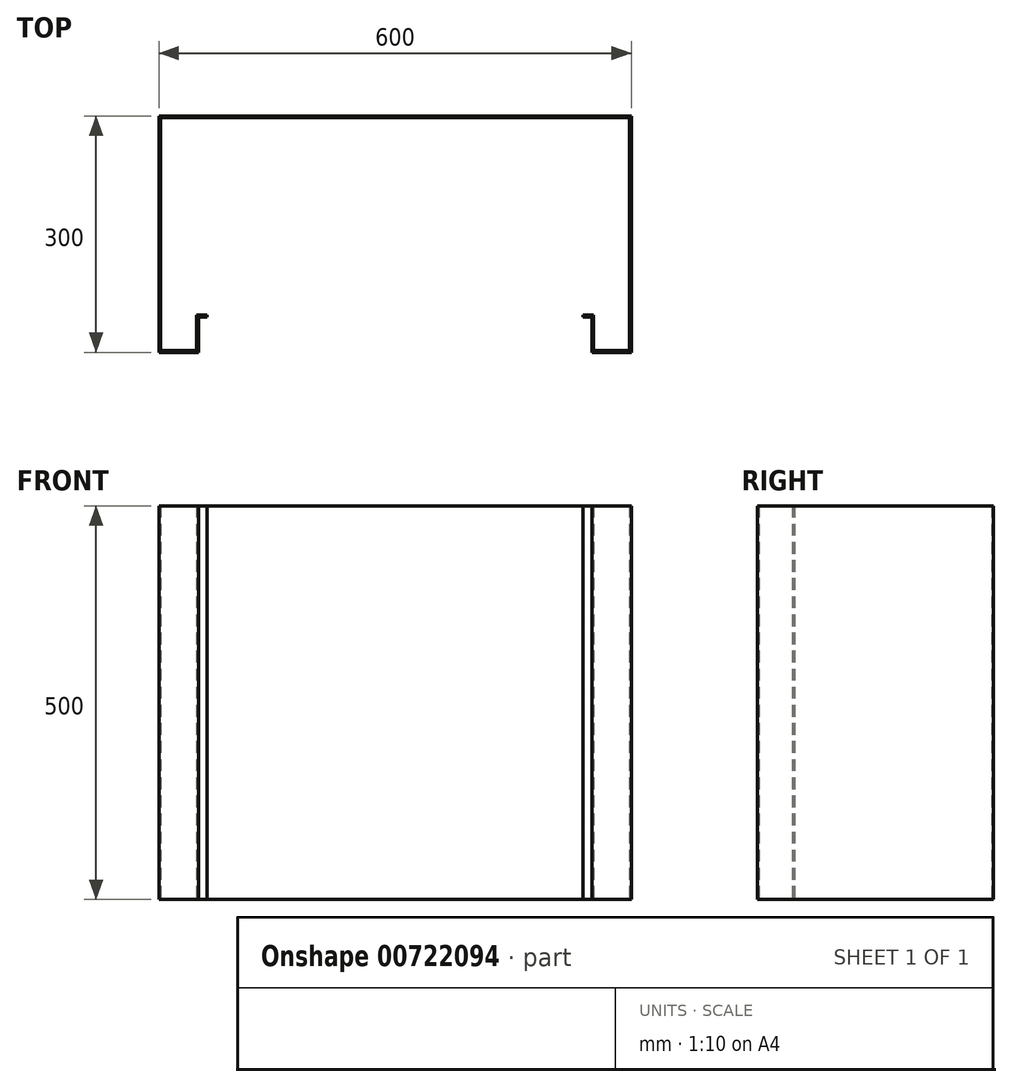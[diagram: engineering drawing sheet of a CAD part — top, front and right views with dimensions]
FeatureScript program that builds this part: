
annotation { "Feature Type Name" : "Feature", "Feature Type Description" : "" }
export const myFeature = defineFeature(function(context is Context, id is Id, definition is map)
    precondition{}
    {
        {
            var Q0;
            Q0=qCreatedBy(makeId("Top.planeOp"),FACE);
            var sketch = newSketch(context, id + "F0", { "sketchPlane" : qUnion([Q0])});
            skLineSegment(sketch, "E0", {"start": v(0, 102.13) * mm, "end": v(-300, 102.13) * mm});
            skLineSegment(sketch, "E1", {"start": v(-300, 102.13) * mm, "end": v(-300, -197.87) * mm});
            skLineSegment(sketch, "E2", {"start": v(-300, -197.87) * mm, "end": v(-250, -197.87) * mm});
            skLineSegment(sketch, "E3", {"start": v(-250, -197.87) * mm, "end": v(-250, -152.87) * mm});
            skLineSegment(sketch, "E4", {"start": v(-250, -152.87) * mm, "end": v(-238.8, -152.87) * mm});
            skLineSegment(sketch, "E5.0", {"start": v(-252, -150.87) * mm, "end": v(-238.8, -150.87) * mm});
            skLineSegment(sketch, "E5.1", {"start": v(-252, -195.87) * mm, "end": v(-252, -150.87) * mm});
            skLineSegment(sketch, "E5.2", {"start": v(-298, -195.87) * mm, "end": v(-252, -195.87) * mm});
            skLineSegment(sketch, "E5.3", {"start": v(-298, 100.13) * mm, "end": v(-298, -195.87) * mm});
            skLineSegment(sketch, "E5.4", {"start": v(0, 100.13) * mm, "end": v(-298, 100.13) * mm});
            skLineSegment(sketch, "E6", {"start": v(-238.8, -152.87) * mm, "end": v(-238.8, -150.87) * mm});
            skLineSegment(sketch, "E7.MirrorCS", {"start": v(252, -150.87) * mm, "end": v(238.8, -150.87) * mm});
            skLineSegment(sketch, "E8.MirrorCS", {"start": v(250, -152.87) * mm, "end": v(238.8, -152.87) * mm});
            skLineSegment(sketch, "E9.MirrorCS", {"start": v(238.8, -152.87) * mm, "end": v(238.8, -150.87) * mm});
            skLineSegment(sketch, "E10.MirrorCS", {"start": v(250, -197.87) * mm, "end": v(250, -152.87) * mm});
            skLineSegment(sketch, "E11.MirrorCS", {"start": v(0, 102.13) * mm, "end": v(300, 102.13) * mm});
            skLineSegment(sketch, "E12.MirrorCS", {"start": v(0, 100.13) * mm, "end": v(298, 100.13) * mm});
            skLineSegment(sketch, "E13.MirrorCS", {"start": v(300, -197.87) * mm, "end": v(250, -197.87) * mm});
            skLineSegment(sketch, "E14.MirrorCS", {"start": v(300, 102.13) * mm, "end": v(300, -197.87) * mm});
            skLineSegment(sketch, "E15.MirrorCS", {"start": v(298, -195.87) * mm, "end": v(252, -195.87) * mm});
            skLineSegment(sketch, "E16.MirrorCS", {"start": v(298, 100.13) * mm, "end": v(298, -195.87) * mm});
            skLineSegment(sketch, "E17.MirrorCS", {"start": v(252, -195.87) * mm, "end": v(252, -150.87) * mm});
            skSolve(sketch);
        }
        {
            var Q0;
            Q0 = qSketchRegion(id + "F0", true);
            extrude(context, id + "F1", {"entities" : qUnion([Q0]), "depth" : 500 * mm, "offsetDistance" : 25 * mm});
        }
    });
